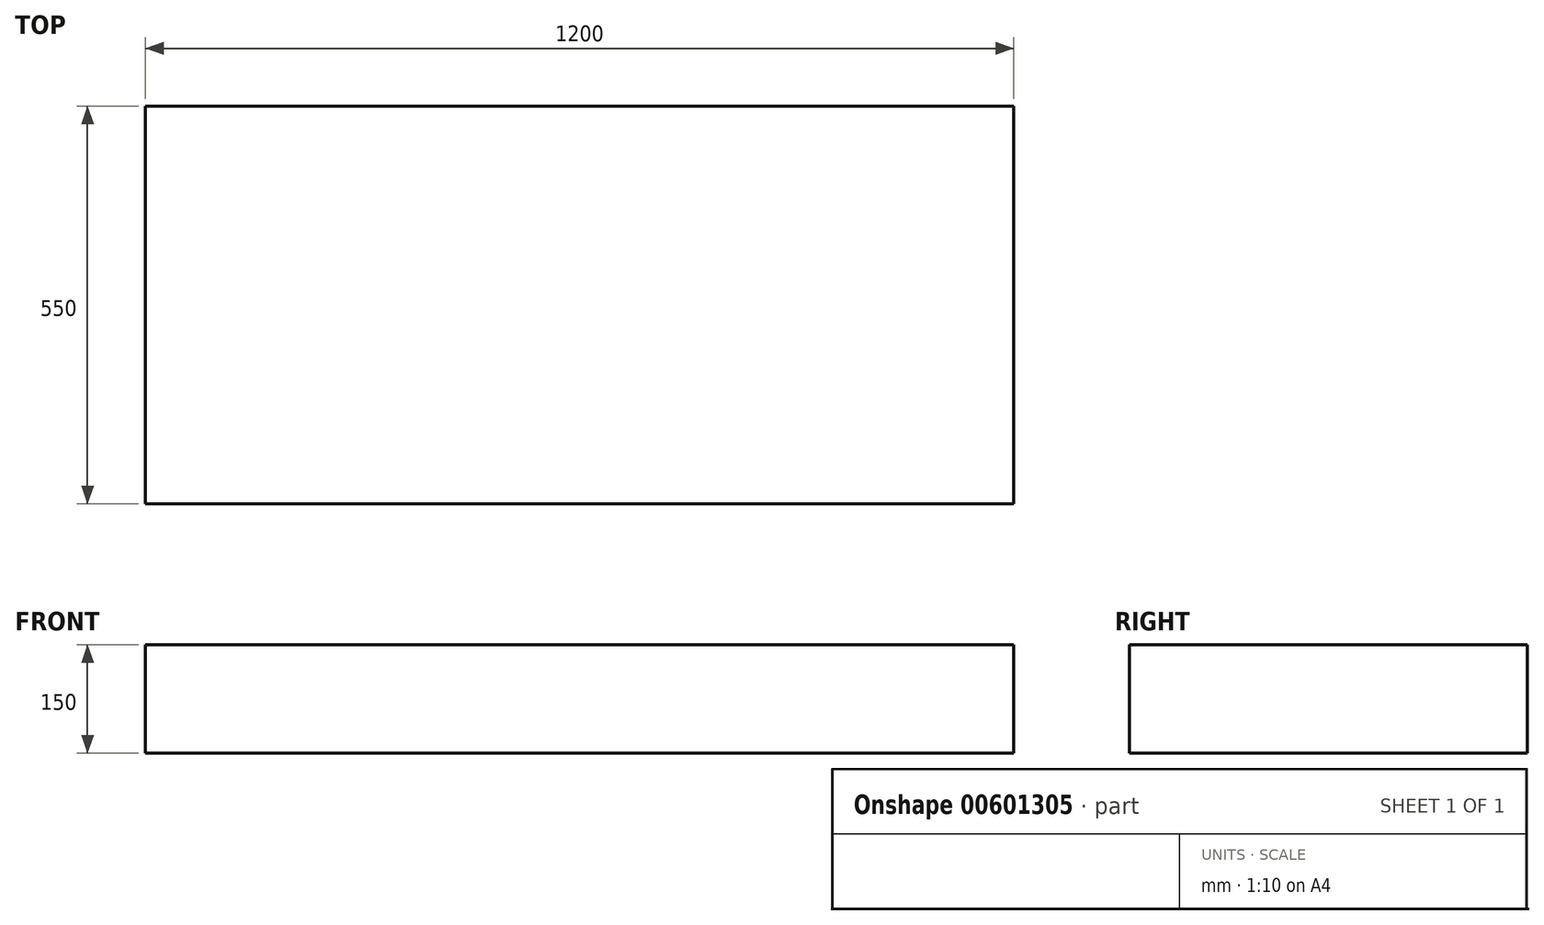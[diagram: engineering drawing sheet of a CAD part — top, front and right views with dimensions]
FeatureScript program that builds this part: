
annotation { "Feature Type Name" : "Feature", "Feature Type Description" : "" }
export const myFeature = defineFeature(function(context is Context, id is Id, definition is map)
    precondition{}
    {
        {
            var Q0;
            Q0=qCreatedBy(makeId("Top.planeOp"),FACE);
            var sketch = newSketch(context, id + "F0", { "sketchPlane" : qUnion([Q0])});
            skLineSegment(sketch, "E0.bottom", {"start": v(0, 0) * mm, "end": v(1200, 0) * mm});
            skLineSegment(sketch, "E0.top", {"start": v(0, 550) * mm, "end": v(1200, 550) * mm});
            skLineSegment(sketch, "E0.left", {"start": v(0, 0) * mm, "end": v(0, 550) * mm});
            skLineSegment(sketch, "E0.right", {"start": v(1200, 0) * mm, "end": v(1200, 550) * mm});
            skSolve(sketch);
        }
        {
            var Q0;
            Q0=qSketchRegion(id+"F0",true);
            extrude(context, id + "F1", {"entities" : qUnion([Q0]), "depth" : 150 * mm, "offsetDistance" : 25 * mm});
        }
    });
